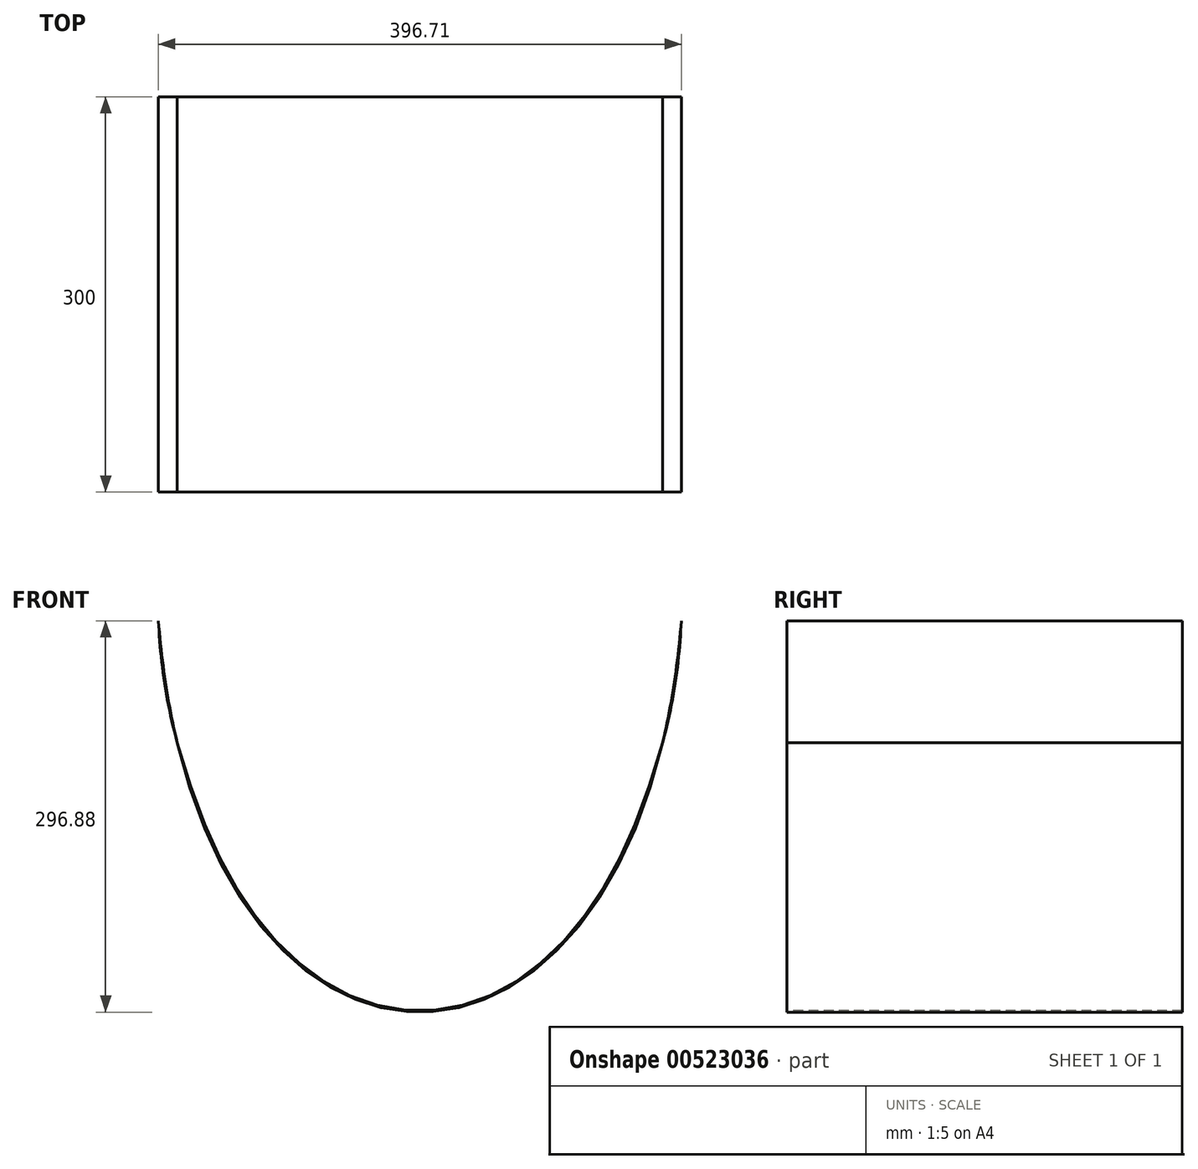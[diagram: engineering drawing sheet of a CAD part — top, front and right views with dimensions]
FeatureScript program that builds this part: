
annotation { "Feature Type Name" : "Feature", "Feature Type Description" : "" }
export const myFeature = defineFeature(function(context is Context, id is Id, definition is map)
    precondition{}
    {
        {
            var Q0;
            Q0=qCreatedBy(makeId("Front.planeOp"),FACE);
            var sketch = newSketch(context, id + "F0", { "sketchPlane" : qUnion([Q0])});
            skFitSpline(sketch, "E0", {"points": [v(-412.35, -11.31) * mm, v(-11.31, -11.31) * mm], "startDerivative": vector(-33.94, -1514.06) * mm, "endDerivative": vector(-33.94, 1514.06) * mm});
            skLineSegment(sketch, "E1.0", {"start": v(13.6, -13.6) * mm, "end": v(1.15, -18.77) * mm});
            skLineSegment(sketch, "E1.1", {"start": v(19.25, 0) * mm, "end": v(13.6, -13.6) * mm});
            skLineSegment(sketch, "E1.2", {"start": v(13.6, 13.6) * mm, "end": v(19.25, 0) * mm});
            skLineSegment(sketch, "E1.3", {"start": v(0, 19.25) * mm, "end": v(13.6, 13.6) * mm});
            skLineSegment(sketch, "E1.4", {"start": v(-13.6, 13.6) * mm, "end": v(0, 19.25) * mm});
            skLineSegment(sketch, "E1.5", {"start": v(-437.28, 13.6) * mm, "end": v(-423.67, 19.25) * mm});
            skLineSegment(sketch, "E1.6", {"start": v(-442.92, 0) * mm, "end": v(-437.28, 13.6) * mm});
            skLineSegment(sketch, "E1.7", {"start": v(-437.28, -13.6) * mm, "end": v(-442.92, 0) * mm});
            skLineSegment(sketch, "E1.8", {"start": v(-424.82, -18.77) * mm, "end": v(-437.28, -13.6) * mm});
            skLineSegment(sketch, "E1.9", {"start": v(-423.67, 19.25) * mm, "end": v(-410.06, 13.6) * mm});
            skLineSegment(sketch, "E1.10", {"start": v(-410.06, 13.6) * mm, "end": v(-404.42, 0) * mm});
            skLineSegment(sketch, "E1.11", {"start": v(-404.42, 0) * mm, "end": v(-409.37, -11.94) * mm});
            skFitSpline(sketch, "E1.12", {"points": [v(-409.36, -11.38) * mm, v(-410.77, -74.26) * mm, v(-402.71, -156.7) * mm, v(-376.82, -242.87) * mm, v(-351.13, -295.63) * mm, v(-320.48, -336.53) * mm, v(-286.2, -365.62) * mm, v(-249.58, -382.98) * mm, v(-211.83, -388.75) * mm, v(-174.1, -382.98) * mm, v(-137.47, -365.62) * mm, v(-103.19, -336.53) * mm, v(-72.54, -295.63) * mm, v(-46.85, -242.87) * mm, v(-20.95, -156.7) * mm, v(-12.9, -74.26) * mm, v(-14.31, -11.38) * mm]});
            skLineSegment(sketch, "E1.13", {"start": v(-14.3, -11.94) * mm, "end": v(-19.25, 0) * mm});
            skLineSegment(sketch, "E1.14", {"start": v(-19.25, 0) * mm, "end": v(-13.6, 13.6) * mm});
            skLineSegment(sketch, "E2", {"start": v(-424.82, -18.77) * mm, "end": v(-412.5, -18.77) * mm});
            skLineSegment(sketch, "E3", {"start": v(1.15, -18.77) * mm, "end": v(-11.18, -18.77) * mm});
            skSolve(sketch);
        }
        {
            var Q0;
            Q0 = qSketchRegion(id + "F0", true);
            extrude(context, id + "F1", {"entities" : qUnion([Q0]), "depth" : 300 * mm, "offsetDistance" : 25 * mm});
        }
        {
            var Q0;
            Q0=makeQuery(id+"F1.opExtrude","CAP_FACE",FACE,{"disambiguationData":[OSD([sQuery(id+"F0.wireOp",EDGE,"E0"),sQuery(id+"F0.wireOp",EDGE,"E1.0"),sQuery(id+"F0.wireOp",EDGE,"E1.1"),sQuery(id+"F0.wireOp",EDGE,"E1.2"),sQuery(id+"F0.wireOp",EDGE,"E1.3"),sQuery(id+"F0.wireOp",EDGE,"E1.4"),sQuery(id+"F0.wireOp",EDGE,"E1.5"),sQuery(id+"F0.wireOp",EDGE,"E1.6"),sQuery(id+"F0.wireOp",EDGE,"E1.7"),sQuery(id+"F0.wireOp",EDGE,"E1.8"),sQuery(id+"F0.wireOp",EDGE,"E1.9"),sQuery(id+"F0.wireOp",EDGE,"E1.10"),sQuery(id+"F0.wireOp",EDGE,"E1.11"),sQuery(id+"F0.wireOp",EDGE,"E1.12"),sQuery(id+"F0.wireOp",EDGE,"E1.13"),sQuery(id+"F0.wireOp",EDGE,"E1.14"),sQuery(id+"F0.wireOp",EDGE,"E2"),sQuery(id+"F0.wireOp",EDGE,"E3")])],"isStart":false});
            var sketch = newSketch(context, id + "F2", { "sketchPlane" : qUnion([Q0])});
            skCircle(sketch, "E4.cCircle", {"center": v(0, 0) * mm, "radius": 16 * mm, "construction": true});
            skLineSegment(sketch, "E4.0", {"start": v(-16, 0) * mm, "end": v(-11.31, 11.31) * mm});
            skLineSegment(sketch, "E4.1", {"start": v(-11.31, 11.31) * mm, "end": v(0, 16) * mm});
            skLineSegment(sketch, "E4.2", {"start": v(0, 16) * mm, "end": v(11.31, 11.31) * mm});
            skLineSegment(sketch, "E4.3", {"start": v(11.31, 11.31) * mm, "end": v(16, 0) * mm});
            skLineSegment(sketch, "E4.4", {"start": v(16, 0) * mm, "end": v(11.31, -11.31) * mm});
            skLineSegment(sketch, "E4.5", {"start": v(11.31, -11.31) * mm, "end": v(0, -16) * mm});
            skLineSegment(sketch, "E4.6", {"start": v(0, -16) * mm, "end": v(-11.31, -11.31) * mm});
            skLineSegment(sketch, "E4.7", {"start": v(-11.31, -11.31) * mm, "end": v(-16, 0) * mm});
            skCircle(sketch, "E5.cCircle", {"center": v(-423.67, 0) * mm, "radius": 16 * mm, "construction": true});
            skLineSegment(sketch, "E5.0", {"start": v(-407.67, 0) * mm, "end": v(-412.35, -11.31) * mm});
            skLineSegment(sketch, "E5.1", {"start": v(-412.35, -11.31) * mm, "end": v(-423.67, -16) * mm});
            skLineSegment(sketch, "E5.2", {"start": v(-423.67, -16) * mm, "end": v(-434.98, -11.31) * mm});
            skLineSegment(sketch, "E5.3", {"start": v(-434.98, -11.31) * mm, "end": v(-439.67, 0) * mm});
            skLineSegment(sketch, "E5.4", {"start": v(-439.67, 0) * mm, "end": v(-434.98, 11.31) * mm});
            skLineSegment(sketch, "E5.5", {"start": v(-434.98, 11.31) * mm, "end": v(-423.67, 16) * mm});
            skLineSegment(sketch, "E5.6", {"start": v(-423.67, 16) * mm, "end": v(-412.35, 11.31) * mm});
            skLineSegment(sketch, "E5.7", {"start": v(-412.35, 11.31) * mm, "end": v(-407.67, 0) * mm});
            skSolve(sketch);
        }
        {
            var Q0;
            Q0 = qSketchRegion(id + "F2", true);
            extrude(context, id + "F3", {"entities" : qUnion([Q0]), "operationType" : NewBodyOperationType.REMOVE, "endBound" : BoundingType.SYMMETRIC, "depth" : 600 * mm, "offsetDistance" : 25 * mm});
        }
    });
